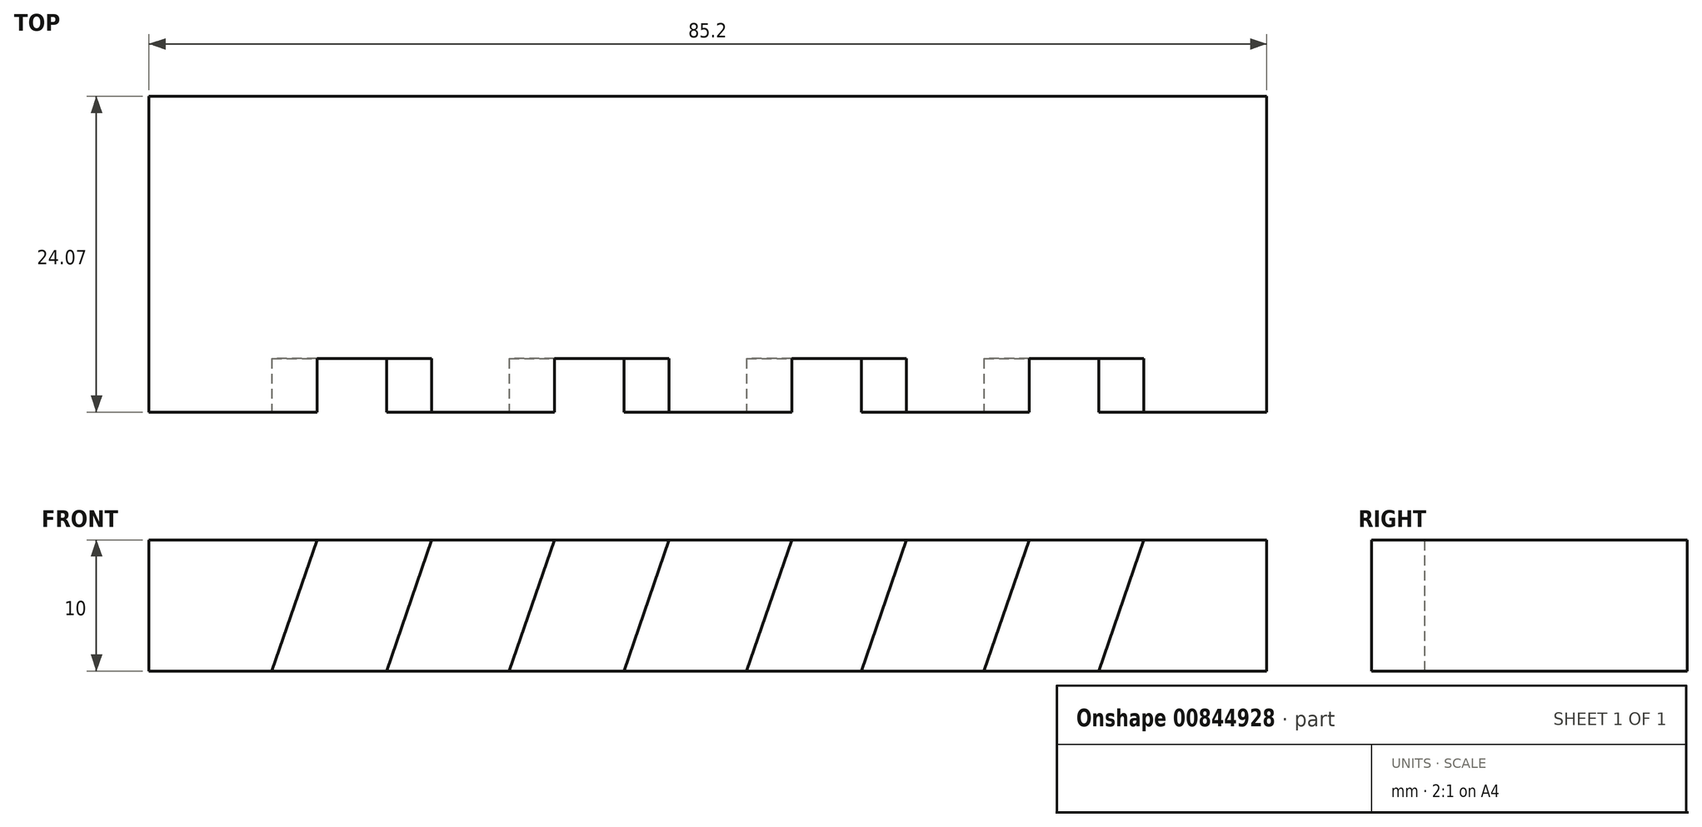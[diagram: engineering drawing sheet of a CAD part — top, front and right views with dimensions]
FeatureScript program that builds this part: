
annotation { "Feature Type Name" : "Feature", "Feature Type Description" : "" }
export const myFeature = defineFeature(function(context is Context, id is Id, definition is map)
    precondition{}
    {
        {
            var Q0;
            Q0=qCreatedBy(makeId("Top.planeOp"),FACE);
            var sketch = newSketch(context, id + "F0", { "sketchPlane" : qUnion([Q0])});
            skLineSegment(sketch, "E0.bottom", {"start": v(-44.1, 9.32) * mm, "end": v(41.1, 9.32) * mm});
            skLineSegment(sketch, "E0.top", {"start": v(-31.3, -10.68) * mm, "end": v(-26, -10.68) * mm});
            skLineSegment(sketch, "E0.left", {"start": v(-44.1, 9.32) * mm, "end": v(-44.1, -10.68) * mm});
            skLineSegment(sketch, "E0.right", {"start": v(41.1, 9.32) * mm, "end": v(41.1, -10.68) * mm});
            skLineSegment(sketch, "E1.top", {"start": v(-44.1, -14.75) * mm, "end": v(-31.3, -14.75) * mm});
            skLineSegment(sketch, "E1.left", {"start": v(-44.1, -10.68) * mm, "end": v(-44.1, -14.75) * mm});
            skLineSegment(sketch, "E1.right", {"start": v(-31.3, -10.68) * mm, "end": v(-31.3, -14.75) * mm});
            skLineSegment(sketch, "E2.top", {"start": v(-26, -14.75) * mm, "end": v(-13.2, -14.75) * mm});
            skLineSegment(sketch, "E2.left", {"start": v(-26, -10.68) * mm, "end": v(-26, -14.75) * mm});
            skLineSegment(sketch, "E2.right", {"start": v(-13.2, -10.68) * mm, "end": v(-13.2, -14.75) * mm});
            skLineSegment(sketch, "E3.top", {"start": v(-7.9, -14.75) * mm, "end": v(4.9, -14.75) * mm});
            skLineSegment(sketch, "E3.left", {"start": v(-7.9, -10.68) * mm, "end": v(-7.9, -14.75) * mm});
            skLineSegment(sketch, "E3.right", {"start": v(4.9, -10.68) * mm, "end": v(4.9, -14.75) * mm});
            skLineSegment(sketch, "E4.top", {"start": v(10.2, -14.75) * mm, "end": v(23, -14.75) * mm});
            skLineSegment(sketch, "E4.left", {"start": v(10.2, -10.68) * mm, "end": v(10.2, -14.75) * mm});
            skLineSegment(sketch, "E4.right", {"start": v(23, -10.68) * mm, "end": v(23, -14.75) * mm});
            skLineSegment(sketch, "E5.top", {"start": v(41.1, -14.75) * mm, "end": v(28.3, -14.75) * mm});
            skLineSegment(sketch, "E5.left", {"start": v(41.1, -10.68) * mm, "end": v(41.1, -14.75) * mm});
            skLineSegment(sketch, "E5.right", {"start": v(28.3, -10.68) * mm, "end": v(28.3, -14.75) * mm});
            skLineSegment(sketch, "E6.trimOffspring", {"start": v(-13.2, -10.68) * mm, "end": v(-7.9, -10.68) * mm});
            skLineSegment(sketch, "E7.trimOffspring", {"start": v(4.9, -10.68) * mm, "end": v(10.2, -10.68) * mm});
            skLineSegment(sketch, "E8.trimOffspring", {"start": v(23, -10.68) * mm, "end": v(28.3, -10.68) * mm});
            skSolve(sketch);
        }
        {
            var Q0;
            Q0=makeQuery(id+"F0.imprint","IMPRINT",FACE,{"disambiguationData":[TD([[makeQuery(id+"F0.imprint","IMPRINT",EDGE,{"derivedFrom":sQuery(id+"F0.wireOp",EDGE,"E0.bottom")}),-1.0]])]});
            extrude(context, id + "F1", {"entities" : qUnion([Q0]), "depth" : 10 * mm, "offsetDistance" : 25 * mm});
        }
        {
            var Q0;
            Q0=makeQuery(id+"F1.opExtrude","CAP_EDGE",EDGE,{"disambiguationData":[OSD([sQuery(id+"F0.wireOp",EDGE,"E1.right")])],"isStart":true});
            chamfer(context, id + "F2", {"entities" : qUnion([Q0]), "chamferType" : ChamferType.OFFSET_ANGLE, "width" : 10 * mm, "oppositeDirection" : true, "angle" : 19 * degree, "tangentPropagation" : true});
        }
        {
            var Q0;
            Q0=makeQuery(id+"F1.opExtrude","CAP_EDGE",EDGE,{"disambiguationData":[OSD([sQuery(id+"F0.wireOp",EDGE,"E2.left")])],"isStart":false});
            chamfer(context, id + "F3", {"entities" : qUnion([Q0]), "chamferType" : ChamferType.OFFSET_ANGLE, "width" : 10 * mm, "oppositeDirection" : true, "angle" : 19 * degree, "tangentPropagation" : true});
        }
        {
            var Q0;
            Q0=makeQuery(id+"F1.opExtrude","CAP_EDGE",EDGE,{"disambiguationData":[OSD([sQuery(id+"F0.wireOp",EDGE,"E2.right")])],"isStart":true});
            chamfer(context, id + "F4", {"entities" : qUnion([Q0]), "chamferType" : ChamferType.OFFSET_ANGLE, "width" : 10 * mm, "oppositeDirection" : true, "angle" : 19 * degree, "tangentPropagation" : true});
        }
        {
            var Q0;
            Q0=makeQuery(id+"F1.opExtrude","CAP_EDGE",EDGE,{"disambiguationData":[OSD([sQuery(id+"F0.wireOp",EDGE,"E3.left")])],"isStart":false});
            chamfer(context, id + "F5", {"entities" : qUnion([Q0]), "chamferType" : ChamferType.OFFSET_ANGLE, "width" : 10 * mm, "oppositeDirection" : true, "angle" : 19 * degree, "tangentPropagation" : true});
        }
        {
            var Q0;
            Q0=makeQuery(id+"F1.opExtrude","CAP_EDGE",EDGE,{"disambiguationData":[OSD([sQuery(id+"F0.wireOp",EDGE,"E3.right")])],"isStart":true});
            chamfer(context, id + "F6", {"entities" : qUnion([Q0]), "chamferType" : ChamferType.OFFSET_ANGLE, "width" : 10 * mm, "oppositeDirection" : true, "angle" : 19 * degree, "tangentPropagation" : true});
        }
        {
            var Q0;
            Q0=makeQuery(id+"F1.opExtrude","CAP_EDGE",EDGE,{"disambiguationData":[OSD([sQuery(id+"F0.wireOp",EDGE,"E4.left")])],"isStart":false});
            chamfer(context, id + "F7", {"entities" : qUnion([Q0]), "chamferType" : ChamferType.OFFSET_ANGLE, "width" : 10 * mm, "oppositeDirection" : true, "angle" : 19 * degree, "tangentPropagation" : true});
        }
        {
            var Q0;
            Q0=makeQuery(id+"F1.opExtrude","CAP_EDGE",EDGE,{"disambiguationData":[OSD([sQuery(id+"F0.wireOp",EDGE,"E4.right")])],"isStart":true});
            chamfer(context, id + "F8", {"entities" : qUnion([Q0]), "chamferType" : ChamferType.OFFSET_ANGLE, "width" : 10 * mm, "oppositeDirection" : true, "angle" : 19 * degree, "tangentPropagation" : true});
        }
        {
            var Q0;
            Q0=makeQuery(id+"F1.opExtrude","CAP_EDGE",EDGE,{"disambiguationData":[OSD([sQuery(id+"F0.wireOp",EDGE,"E5.right")])],"isStart":false});
            chamfer(context, id + "F9", {"entities" : qUnion([Q0]), "chamferType" : ChamferType.OFFSET_ANGLE, "width" : 10 * mm, "oppositeDirection" : true, "angle" : 19 * degree, "tangentPropagation" : true});
        }
    });
